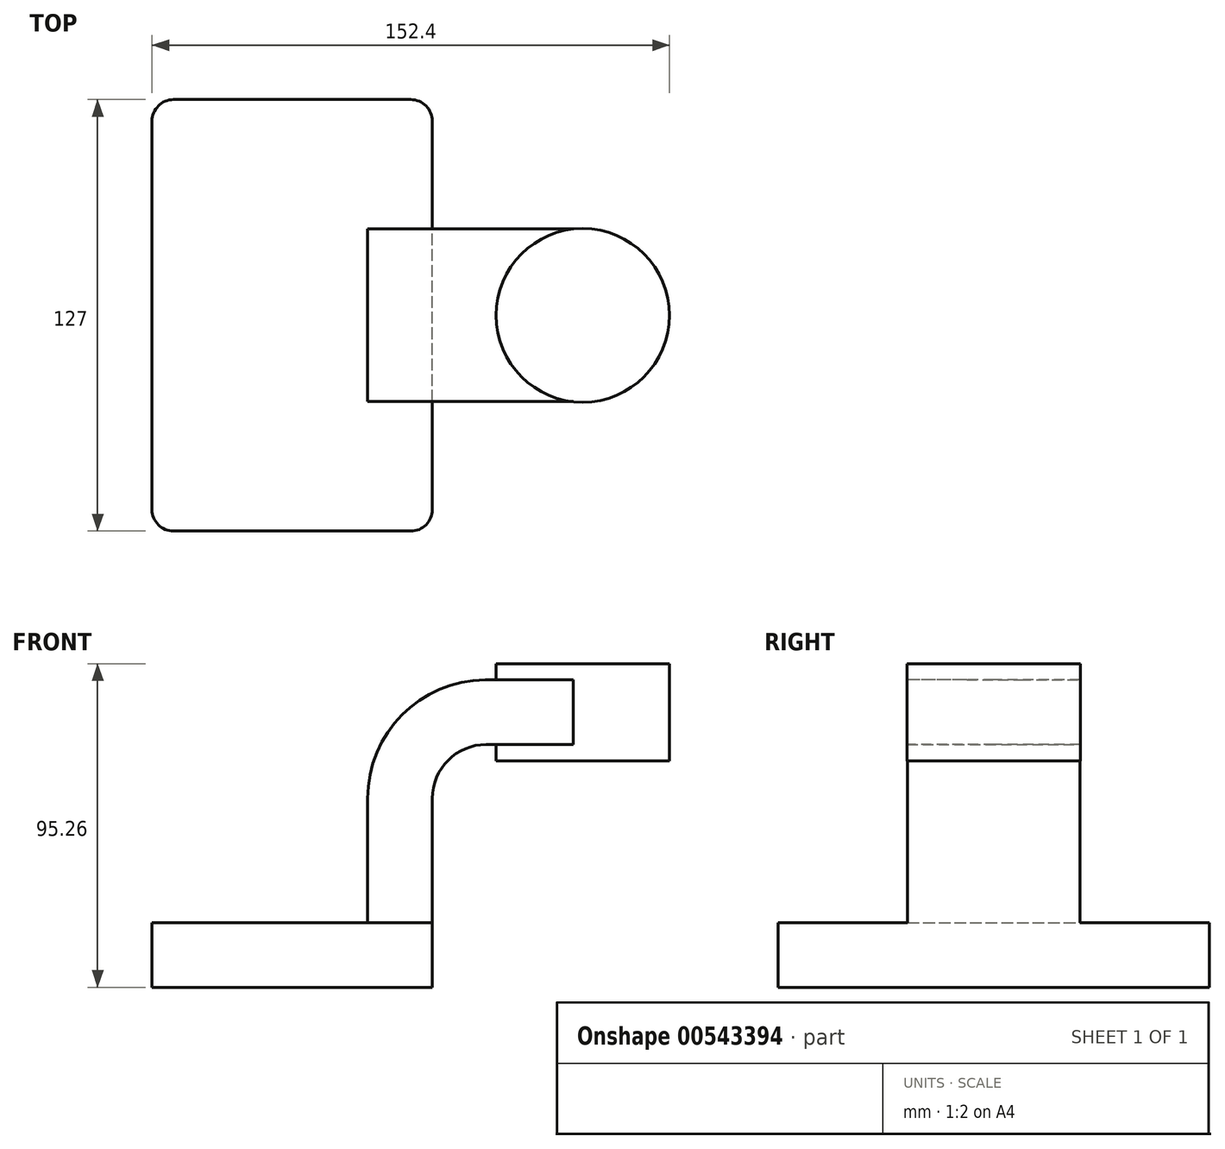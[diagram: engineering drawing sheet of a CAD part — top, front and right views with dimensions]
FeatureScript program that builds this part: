
annotation { "Feature Type Name" : "Feature", "Feature Type Description" : "" }
export const myFeature = defineFeature(function(context is Context, id is Id, definition is map)
    precondition{}
    {
        {
            var Q0;
            Q0=qCreatedBy(makeId("Front.planeOp"),FACE);
            var sketch = newSketch(context, id + "F0", { "sketchPlane" : qUnion([Q0])});
            skLineSegment(sketch, "E0.bottom", {"start": v(-41.28, 9.52) * mm, "end": v(41.28, 9.53) * mm});
            skLineSegment(sketch, "E0.top", {"start": v(-41.28, -9.53) * mm, "end": v(41.28, -9.53) * mm});
            skLineSegment(sketch, "E0.left", {"start": v(-41.28, 9.52) * mm, "end": v(-41.27, -9.53) * mm});
            skLineSegment(sketch, "E0.right", {"start": v(41.28, 9.53) * mm, "end": v(41.28, -9.52) * mm});
            skPoint(sketch, "E0.middle", {"position": v(0, 0) * mm});
            skLineSegment(sketch, "E1.bottom", {"start": v(60.33, 57.15) * mm, "end": v(111.12, 57.15) * mm});
            skLineSegment(sketch, "E1.top", {"start": v(60.33, 85.73) * mm, "end": v(111.12, 85.73) * mm});
            skLineSegment(sketch, "E1.left", {"start": v(60.33, 57.15) * mm, "end": v(60.32, 85.72) * mm});
            skLineSegment(sketch, "E1.right", {"start": v(111.12, 57.15) * mm, "end": v(111.12, 85.73) * mm});
            skPoint(sketch, "E1.middle", {"position": v(85.72, 71.44) * mm});
            skLineSegment(sketch, "E2", {"start": v(41.27, 9.53) * mm, "end": v(41.27, 46.05) * mm});
            skArc(sketch, "E3", {"start": v(41.27, 46.05) * mm, "mid": v(45.92, 57.28) * mm, "end": v(57.15, 61.93) * mm});
            skLineSegment(sketch, "E4", {"start": v(57.15, 61.93) * mm, "end": v(85.57, 61.93) * mm});
            skLineSegment(sketch, "E5.0", {"start": v(57.15, 80.98) * mm, "end": v(85.57, 80.98) * mm});
            skArc(sketch, "E5.1", {"start": v(22.22, 46.05) * mm, "mid": v(32.45, 70.75) * mm, "end": v(57.15, 80.98) * mm});
            skLineSegment(sketch, "E5.2", {"start": v(22.22, 9.53) * mm, "end": v(22.22, 46.05) * mm});
            skLineSegment(sketch, "E6", {"start": v(85.57, 57.15) * mm, "end": v(85.57, 85.73) * mm});
            skFitSpline(sketch, "E7", {"points": [v(57.15, 80.98) * mm, v(-41.28, 9.53) * mm], "startDerivative": vector(-296.6, -1.1) * mm, "endDerivative": vector(0.35, -88.54) * mm});
            skSolve(sketch);
        }
        {
            var Q0;
            Q0=makeQuery(id+"F0.imprint","IMPRINT",FACE,{"disambiguationData":[TD([[makeQuery(id+"F0.imprint","IMPRINT",EDGE,{"derivedFrom":sQuery(id+"F0.wireOp",EDGE,"E0.top")}),1.0]])]});
            extrude(context, id + "F1", {"entities" : qUnion([Q0]), "endBound" : BoundingType.SYMMETRIC, "depth" : 127 * mm, "offsetDistance" : 25.4 * mm});
        }
        {
            var Q0;
            {var subQ1=sQuery(id+"F0.wireOp",EDGE,"E2");Q0=makeQuery(id+"F0.imprint","IMPRINT",FACE,{"disambiguationData":[TD([[makeQuery(id+"F0.imprint","IMPRINT",EDGE,{"derivedFrom":subQ1}),1.0]])]});}
            var Q1;
            {var subQ0=sQuery(id+"F0.wireOp",EDGE,"E4");var subQ1=sQuery(id+"F0.wireOp",EDGE,"E1.left");var subQ2=makeQuery(id+"F0.imprint","INTERSECT",VERTEX,{"derivedFrom":[subQ1,subQ0]});Q1=makeQuery(id+"F0.imprint","IMPRINT",FACE,{"disambiguationData":[TD([[makeQuery(id+"F0.imprint","IMPRINT",EDGE,{"disambiguationData":[TD([[subQ2,-1.0]])],"derivedFrom":subQ1}),-1.0]])]});}
            extrude(context, id + "F2", {"entities" : qUnion([Q0, Q1]), "operationType" : NewBodyOperationType.ADD, "endBound" : BoundingType.SYMMETRIC, "depth" : 50.8 * mm, "offsetDistance" : 25.4 * mm});
        }
        {
            var Q0;
            {var subQ4=sQuery(id+"F0.wireOp",EDGE,"E5.1");Q0=makeQuery(id+"F0.imprint","IMPRINT",FACE,{"disambiguationData":[TD([[makeQuery(id+"F0.imprint","IMPRINT",EDGE,{"derivedFrom":subQ4}),1.0]])]});}
            extrude(context, id + "F3", {"entities" : qUnion([Q0]), "operationType" : NewBodyOperationType.ADD, "endBound" : BoundingType.SYMMETRIC, "depth" : 15.88 * mm, "offsetDistance" : 25.4 * mm});
        }
        {
            var Q0;
            {var subQ0=sQuery(id+"F0.wireOp",EDGE,"E1.right");Q0=makeQuery(id+"F0.imprint","IMPRINT",FACE,{"disambiguationData":[TD([[makeQuery(id+"F0.imprint","IMPRINT",EDGE,{"derivedFrom":subQ0}),1.0]])]});}
            var Q1;
            Q1=sQuery(id+"F0.wireOp",EDGE,"E6");
            revolve(context, id + "F4", {"operationType" : NewBodyOperationType.ADD, "entities" : qUnion([Q0]), "axis" : qUnion([Q1]), "revolveType" : RevolveType.FULL});
        }
        {
            var Q0;
            Q0=makeQuery(id+"F1.opExtrude","CAP_EDGE",EDGE,{"disambiguationData":[OSD([sQuery(id+"F0.wireOp",EDGE,"E0.right")])],"isStart":false});
            var Q1;
            Q1=makeQuery(id+"F1.opExtrude","CAP_EDGE",EDGE,{"disambiguationData":[OSD([sQuery(id+"F0.wireOp",EDGE,"E0.right")])],"isStart":true});
            var Q2;
            Q2=makeQuery(id+"F1.opExtrude","CAP_EDGE",EDGE,{"disambiguationData":[OSD([sQuery(id+"F0.wireOp",EDGE,"E0.left")])],"isStart":true});
            var Q3;
            Q3=makeQuery(id+"F1.opExtrude","CAP_EDGE",EDGE,{"disambiguationData":[OSD([sQuery(id+"F0.wireOp",EDGE,"E0.left")])],"isStart":false});
            fillet(context, id + "F5", {"entities" : qUnion([Q0, Q1, Q2, Q3]), "radius" : 6.35 * mm, "tangentPropagation" : true, "allowEdgeOverflow" : false});
        }
    });
